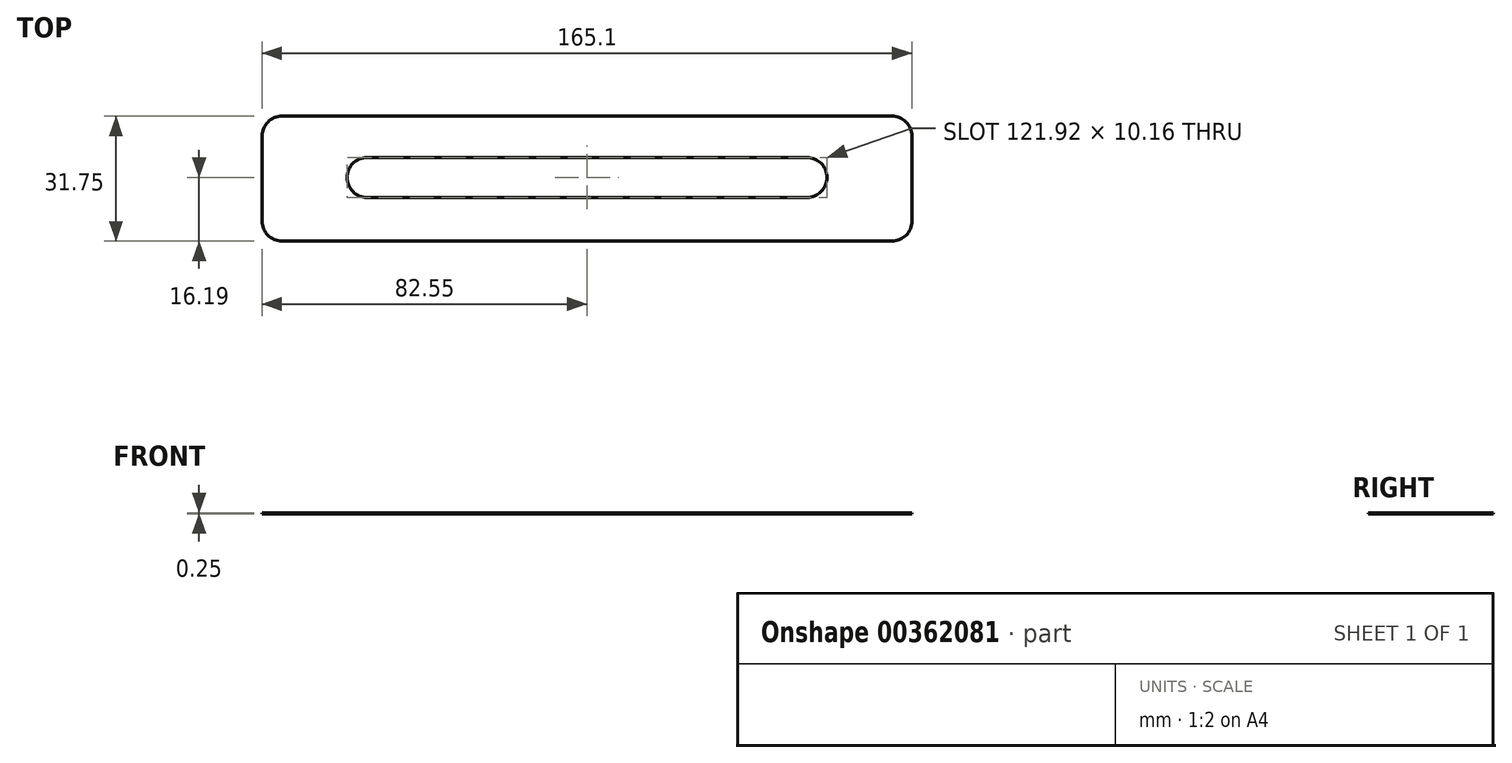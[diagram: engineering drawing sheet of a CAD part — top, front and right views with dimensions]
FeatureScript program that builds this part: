
annotation { "Feature Type Name" : "Feature", "Feature Type Description" : "" }
export const myFeature = defineFeature(function(context is Context, id is Id, definition is map)
    precondition{}
    {
        {
            assignVariable(context, id + "F0", {"name" : "MT", "anyValue" : .25});
        }
        {
            var Q0;
            Q0=qCreatedBy(makeId("Top.planeOp"),FACE);
            var sketch = newSketch(context, id + "F1", { "sketchPlane" : qUnion([Q0])});
            skLineSegment(sketch, "E0.bottom", {"start": v(-82.55, 15.56) * mm, "end": v(82.55, 15.56) * mm});
            skLineSegment(sketch, "E0.top", {"start": v(-82.55, -16.2) * mm, "end": v(82.55, -16.2) * mm});
            skLineSegment(sketch, "E0.left", {"start": v(-82.55, 15.56) * mm, "end": v(-82.55, -16.2) * mm});
            skLineSegment(sketch, "E0.right", {"start": v(82.55, 15.56) * mm, "end": v(82.55, -16.2) * mm});
            skArc(sketch, "E1", {"start": v(-55.88, 5.08) * mm, "mid": v(-60.96, 0) * mm, "end": v(-55.88, -5.08) * mm});
            skLineSegment(sketch, "E2", {"start": v(-55.88, 5.08) * mm, "end": v(0, 5.08) * mm});
            skLineSegment(sketch, "E3", {"start": v(-55.88, -5.08) * mm, "end": v(0, -5.08) * mm});
            skLineSegment(sketch, "E4", {"start": v(-55.88, 5.23) * mm, "end": v(-55.88, -5.92) * mm, "construction": true});
            skLineSegment(sketch, "E5.MirrorCS", {"start": v(55.88, 5.08) * mm, "end": v(0, 5.08) * mm});
            skLineSegment(sketch, "E6.MirrorCS", {"start": v(55.88, -5.08) * mm, "end": v(0, -5.08) * mm});
            skArc(sketch, "E7.MirrorCS", {"start": v(55.88, 5.08) * mm, "mid": v(60.96, 0) * mm, "end": v(55.88, -5.08) * mm});
            skSolve(sketch);
        }
        {
            var Q0;
            Q0 = qSketchRegion(id + "F1", true);
            extrude(context, id + "F2", {"entities" : qUnion([Q0]), "depth" : (getVariable(context, 'MT')) * mm});
        }
        {
            var Q0;
            Q0=makeQuery(id+"F2.opExtrude","SWEPT_EDGE",EDGE,{"disambiguationData":[OSD([sQuery(id+"F1.wireOp",EDGE,"E0.bottom"),sQuery(id+"F1.wireOp",EDGE,"E0.left")])]});
            var Q1;
            Q1=makeQuery(id+"F2.opExtrude","SWEPT_EDGE",EDGE,{"disambiguationData":[OSD([sQuery(id+"F1.wireOp",EDGE,"E0.top"),sQuery(id+"F1.wireOp",EDGE,"E0.left")])]});
            var Q2;
            Q2=makeQuery(id+"F2.opExtrude","SWEPT_EDGE",EDGE,{"disambiguationData":[OSD([sQuery(id+"F1.wireOp",EDGE,"E0.bottom"),sQuery(id+"F1.wireOp",EDGE,"E0.right")])]});
            var Q3;
            Q3=makeQuery(id+"F2.opExtrude","SWEPT_EDGE",EDGE,{"disambiguationData":[OSD([sQuery(id+"F1.wireOp",EDGE,"E0.top"),sQuery(id+"F1.wireOp",EDGE,"E0.right")])]});
            fillet(context, id + "F3", {"entities" : qUnion([Q0, Q1, Q2, Q3]), "radius" : 5.08 * mm, "tangentPropagation" : true, "allowEdgeOverflow" : false});
        }
    });
